# Revit family: PRD_FrankeWS_WCFlshngVlvs_WCControl_AT3O0051
name_source: partatom
category: Plumbing Fixtures
revit_build: Autodesk Revit 2018 (Build: 20190510_1515(x64)
units: mm (PartAtom-declared; Revit-internal decimal feet)

## family parameters
Cut with Voids When Loaded = No
Host = Face
OmniClass Number = 23.45.05.14.99
OmniClass Title = Other Sanitary Washing Plumbing Fixtures
Part Type = Normal
Room Calculation Point = No
Round Connector Dimension = Use Diameter
Shared = No

## types (1)
- AT3O0051
    AssetType = Fixed
    BIMObjectName = PRD_AR_WCFlushingValves_WCControl_AT3O0051
    Category = Pr_40_20_93_91, WC flushing valves
    Color = Stainless steel
    Default Elevation = 1000 mm  [stored 3.28084 ft]
    Description = AQUATIMER - A3000 open electronically controlled WC control for concealed cistern with option for external controlling options such as setting the parameters and comunciation via ECC function controller. Consisting of waterproof electronic module with additional input for sensor switches (provided by customer), maximum distance to electronic module 5 m, servo motor, two waterproof electric t-junctions for connection to system cable, frame and stainless steel cover plate with integrated piezo switch and concealed screw connection, 24 V DC.
    DurationUnit = year
    FlushValveMaterial = PRD_AR_StainlessSteel_SatinFinished
    FlushingRate = 0.0 L/s
    GrossWeight = 1.04 kg
    HasIntegralShutOffDevice = Yes
    IfcExportAs = IfcValveType
    IfcExportType = FLUSHING
    IsHighPressure = No
    Manufacturer = KWC Group AG
    ManufacturerName = KWC Group AG
    ManufacturerURL = www.kwc.com
    Material = Stainless steel
    Model = AT3O0051
    ModelNumber = 2030021142
    ModelReference = AT3O0051
    NBSDescription = WC flushing valves
    NBSReference = 45-35-70/389
    Name = WC control AT3O0051
    NetWeight = 0.93 kg
    NominalHeight = 0 mm  [stored 0 ft]
    NominalLength = 0 mm  [stored 0 ft]
    NominalWidth = 0 mm  [stored 0 ft]
    Operation = Sensor
    ProductInformation = https://pim.kwc.com
    URL = www.kwc.com
    Uniclass2015Code = Pr_40_20_93_91
    Uniclass2015Title = WC flushing valves
    Uniclass2015Version = Products v1.7
    Version = 1
    WarrantyDurationUnit = year

note: [stored X ft] marks values corroborated as IEEE doubles in the binary element streams (Revit-internal decimal feet)

## geometry (parser evidence)
native form markers: Sweep x2
no freeform markers — native parametric forms only
